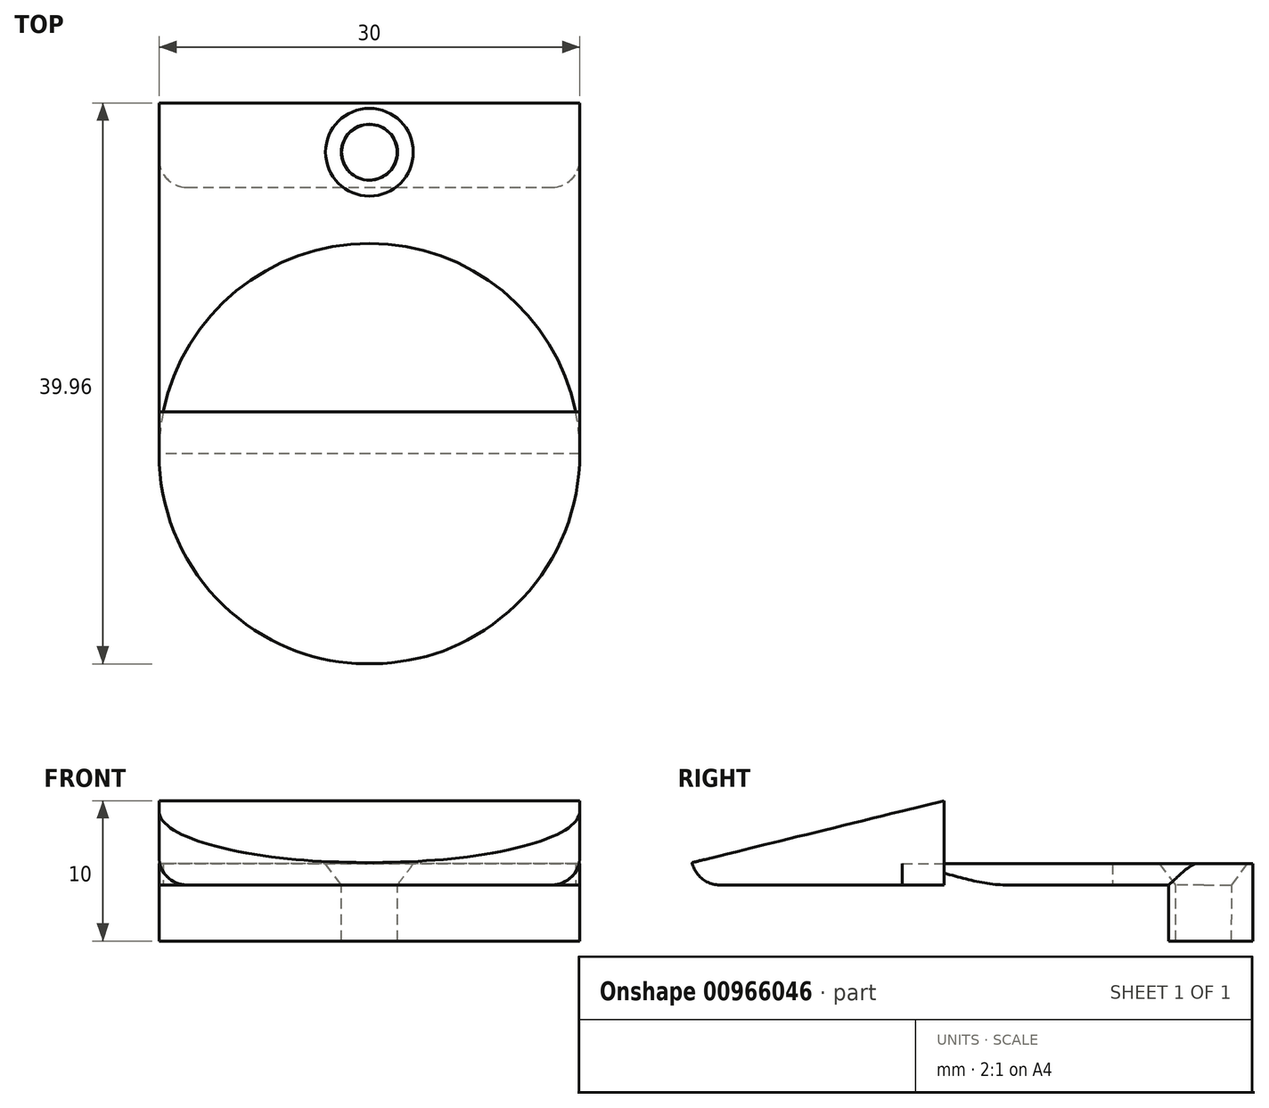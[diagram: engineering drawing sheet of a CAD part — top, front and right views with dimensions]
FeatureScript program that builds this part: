
annotation { "Feature Type Name" : "Feature", "Feature Type Description" : "" }
export const myFeature = defineFeature(function(context is Context, id is Id, definition is map)
    precondition{}
    {
        {
            var Q0;
            Q0=qCreatedBy(makeId("Top.planeOp"),FACE);
            var sketch = newSketch(context, id + "F0", { "sketchPlane" : qUnion([Q0])});
            skLineSegment(sketch, "E0.bottom", {"start": v(15, -12.5) * mm, "end": v(-15, -12.5) * mm});
            skLineSegment(sketch, "E0.top", {"start": v(15, 12.5) * mm, "end": v(-15, 12.5) * mm});
            skLineSegment(sketch, "E0.left", {"start": v(15, -12.5) * mm, "end": v(15, 12.5) * mm});
            skLineSegment(sketch, "E0.right", {"start": v(-15, -12.5) * mm, "end": v(-15, 12.5) * mm});
            skPoint(sketch, "E0.middle", {"position": v(0, 0) * mm});
            skCircle(sketch, "E1", {"center": v(0, -12.5) * mm, "radius": 15 * mm});
            skLineSegment(sketch, "E2.bottom", {"start": v(-15, 12.5) * mm, "end": v(15, 12.5) * mm});
            skLineSegment(sketch, "E2.top", {"start": v(-15, -9.5) * mm, "end": v(15, -9.5) * mm});
            skLineSegment(sketch, "E2.left", {"start": v(-15, 12.5) * mm, "end": v(-15, -9.5) * mm});
            skLineSegment(sketch, "E2.right", {"start": v(15, 12.5) * mm, "end": v(15, -9.5) * mm});
            skLineSegment(sketch, "E3.top", {"start": v(-15, 6.5) * mm, "end": v(15, 6.5) * mm});
            skLineSegment(sketch, "E3.left", {"start": v(-15, 12.5) * mm, "end": v(-15, 6.5) * mm});
            skLineSegment(sketch, "E3.right", {"start": v(15, 12.5) * mm, "end": v(15, 6.5) * mm});
            skSolve(sketch);
        }
        {
            var Q0;
            {var subQ1=sQuery(id+"F0.wireOp",EDGE,"E0.top");Q0=makeQuery(id+"F0.imprint","IMPRINT",FACE,{"disambiguationData":[TD([[makeQuery(id+"F0.imprint","IMPRINT",EDGE,{"derivedFrom":subQ1}),1.0]])]});}
            var Q1;
            {var subQ0=sQuery(id+"F0.wireOp",EDGE,"E2.top");var subQ1=sQuery(id+"F0.wireOp",EDGE,"E1");var subQ2=makeQuery(id+"F0.imprint","INTERSECT",VERTEX,{"disambiguationData":[OD(0.0)],"derivedFrom":[subQ1,subQ0]});Q1=makeQuery(id+"F0.imprint","IMPRINT",FACE,{"disambiguationData":[TD([[makeQuery(id+"F0.imprint","IMPRINT",EDGE,{"disambiguationData":[TD([[subQ2,1.0]])],"derivedFrom":subQ1}),1.0]])]});}
            var Q2;
            {var subQ5=sQuery(id+"F0.wireOp",EDGE,"E3.top");Q2=makeQuery(id+"F0.imprint","IMPRINT",FACE,{"disambiguationData":[TD([[makeQuery(id+"F0.imprint","IMPRINT",EDGE,{"derivedFrom":subQ5}),-1.0]])]});}
            extrude(context, id + "F1", {"entities" : qUnion([Q0, Q1, Q2]), "depth" : 1.5 * mm, "offsetDistance" : 25 * mm});
        }
        {
            var Q0;
            {var subQ0=sQuery(id+"F0.wireOp",EDGE,"E0.bottom");Q0=makeQuery(id+"F0.imprint","IMPRINT",FACE,{"disambiguationData":[TD([[makeQuery(id+"F0.imprint","IMPRINT",EDGE,{"derivedFrom":subQ0}),-1.0]])]});}
            var Q1;
            {var subQ1=sQuery(id+"F0.wireOp",EDGE,"E0.left");var subQ3=sQuery(id+"F0.wireOp",EDGE,"E2.top");var subQ4=makeQuery(id+"F0.imprint","INTERSECT",VERTEX,{"derivedFrom":[subQ1,subQ3]});Q1=makeQuery(id+"F0.imprint","IMPRINT",FACE,{"disambiguationData":[TD([[makeQuery(id+"F0.imprint","IMPRINT",EDGE,{"disambiguationData":[TD([[subQ4,1.0]])],"derivedFrom":subQ3}),-1.0]])]});}
            var Q2;
            {var subQ0=sQuery(id+"F0.wireOp",EDGE,"E0.bottom");Q2=makeQuery(id+"F0.imprint","IMPRINT",FACE,{"disambiguationData":[TD([[makeQuery(id+"F0.imprint","IMPRINT",EDGE,{"derivedFrom":subQ0}),1.0]])]});}
            var Q3;
            {var subQ1=sQuery(id+"F0.wireOp",EDGE,"E0.right");var subQ3=sQuery(id+"F0.wireOp",EDGE,"E2.top");var subQ4=makeQuery(id+"F0.imprint","INTERSECT",VERTEX,{"derivedFrom":[subQ1,subQ3]});Q3=makeQuery(id+"F0.imprint","IMPRINT",FACE,{"disambiguationData":[TD([[makeQuery(id+"F0.imprint","IMPRINT",EDGE,{"disambiguationData":[TD([[subQ4,-1.0]])],"derivedFrom":subQ3}),-1.0]])]});}
            extrude(context, id + "F2", {"entities" : qUnion([Q0, Q1, Q2, Q3]), "depth" : 6 * mm, "offsetDistance" : 25 * mm});
        }
        {
            var Q0;
            Q0=makeQuery(id+"F2.opExtrude","SWEPT_FACE",FACE,{"disambiguationData":[OSD([sQuery(id+"F0.wireOp",EDGE,"E0.right")])]});
            var sketch = newSketch(context, id + "F3", { "sketchPlane" : qUnion([Q0])});
            skLineSegment(sketch, "E4", {"start": v(9.5, 6) * mm, "end": v(33.91, 0) * mm});
            skLineSegment(sketch, "E5", {"start": v(33.91, 0) * mm, "end": v(33.91, 6) * mm});
            skLineSegment(sketch, "E6", {"start": v(33.91, 6) * mm, "end": v(9.5, 6) * mm});
            skSolve(sketch);
        }
        {
            var Q0;
            {var subQ0=sQuery(id+"F3.wireOp",EDGE,"E6");var subQ1=sQuery(id+"F3.wireOp",EDGE,"E4");var subQ2=sQuery(id+"F0.wireOp",EDGE,"E0.right");var subQ3=makeQuery(id+"F3.imprint","INTERSECT",VERTEX,{"derivedFrom":[makeQuery(id+"F2.opExtrude","SWEPT_EDGE",EDGE,{"disambiguationData":[OSD([subQ2,sQuery(id+"F0.wireOp",EDGE,"E2.top")])]}),subQ1,subQ0]});Q0=makeQuery(id+"F3.imprint","IMPRINT",FACE,{"disambiguationData":[TD([[makeQuery(id+"F3.imprint","IMPRINT",EDGE,{"disambiguationData":[TD([[subQ3,-1.0]])],"derivedFrom":subQ1}),1.0]])]});}
            var Q1;
            {var subQ0=sQuery(id+"F3.wireOp",EDGE,"E5");Q1=makeQuery(id+"F3.imprint","IMPRINT",FACE,{"disambiguationData":[TD([[makeQuery(id+"F3.imprint","IMPRINT",EDGE,{"derivedFrom":subQ0}),1.0]])]});}
            extrude(context, id + "F4", {"entities" : qUnion([Q0, Q1]), "operationType" : NewBodyOperationType.REMOVE, "oppositeDirection" : true, "depth" : 30 * mm, "offsetDistance" : 25 * mm});
        }
        {
            var Q0;
            Q0=qCreatedBy(makeId("Right.planeOp"),FACE);
            var sketch = newSketch(context, id + "F5", { "sketchPlane" : qUnion([Q0])});
            skLineSegment(sketch, "E7", {"start": v(0, 0) * mm, "end": v(9, 0) * mm});
            skLineSegment(sketch, "E8", {"start": v(9, 0) * mm, "end": v(9, 2) * mm});
            skLineSegment(sketch, "E9", {"start": v(9, 2) * mm, "end": v(12.5, 2) * mm});
            skLineSegment(sketch, "E10", {"start": v(12.5, 2) * mm, "end": v(11, 0) * mm});
            skLineSegment(sketch, "E11", {"start": v(9, 0) * mm, "end": v(9, -4) * mm});
            skLineSegment(sketch, "E12", {"start": v(9, -4) * mm, "end": v(11, -4) * mm});
            skLineSegment(sketch, "E13", {"start": v(11, -4) * mm, "end": v(11, 0) * mm});
            skSolve(sketch);
        }
        {
            var Q0;
            {var subQ0=sQuery(id+"F0.wireOp",EDGE,"E0.top");Q0=makeQuery(id+"F0.imprint","IMPRINT",FACE,{"disambiguationData":[TD([[makeQuery(id+"F0.imprint","IMPRINT",EDGE,{"derivedFrom":subQ0}),1.0]])]});}
            extrude(context, id + "F6", {"entities" : qUnion([Q0]), "operationType" : NewBodyOperationType.ADD, "oppositeDirection" : true, "depth" : 4 * mm, "offsetDistance" : 25 * mm});
        }
        {
            var Q0;
            Q0=makeQuery(id+"F5.imprint","IMPRINT",FACE,{"disambiguationData":[TD([[makeQuery(id+"F5.imprint","IMPRINT",EDGE,{"derivedFrom":sQuery(id+"F5.wireOp",EDGE,"E8")}),-1.0]])]});
            var Q1;
            Q1=sQuery(id+"F5.wireOp",EDGE,"E11");
            revolve(context, id + "F7", {"operationType" : NewBodyOperationType.REMOVE, "surfaceOperationType" : NewSurfaceOperationType.NEW, "entities" : qUnion([Q0]), "axis" : qUnion([Q1]), "revolveType" : RevolveType.FULL, "oppositeDirection" : true});
        }
        {
            var Q0;
            Q0=makeQuery(id+"F4.boolean.opBoolean","COPY",EDGE,{"derivedFrom":makeQuery(id+"F4.opExtrude","CAP_EDGE",EDGE,{"disambiguationData":[OSD([sQuery(id+"F3.wireOp",EDGE,"E4")])],"isStart":true})});
            var Q1;
            Q1=makeQuery(id+"F2.opExtrude","CAP_EDGE",EDGE,{"disambiguationData":[OSD([sQuery(id+"F0.wireOp",EDGE,"E0.right")])],"isStart":true});
            var Q2;
            Q2=makeQuery(id+"F1.opExtrude","CAP_EDGE",EDGE,{"disambiguationData":[OSD([sQuery(id+"F0.wireOp",EDGE,"E0.right")])],"isStart":true});
            var Q3;
            Q3=makeQuery(id+"F1.opExtrude","CAP_EDGE",EDGE,{"disambiguationData":[OSD([sQuery(id+"F0.wireOp",EDGE,"E0.left")])],"isStart":true});
            var Q4;
            Q4=makeQuery(id+"F6.opExtrude","SWEPT_EDGE",EDGE,{"disambiguationData":[OSD([sQuery(id+"F0.wireOp",EDGE,"E0.right"),sQuery(id+"F0.wireOp",EDGE,"E3.top")])]});
            var Q5;
            Q5=makeQuery(id+"F6.opExtrude","SWEPT_EDGE",EDGE,{"disambiguationData":[OSD([sQuery(id+"F0.wireOp",EDGE,"E0.left"),sQuery(id+"F0.wireOp",EDGE,"E3.top")])]});
            fillet(context, id + "F8", {"entities" : qUnion([Q0, Q1, Q2, Q3, Q4, Q5]), "tangentPropagation" : true, "radius" : 2 * mm, "defaultsChanged" : false, "vertexSettings" : [], "allowEdgeOverflow" : false});
        }
    });
